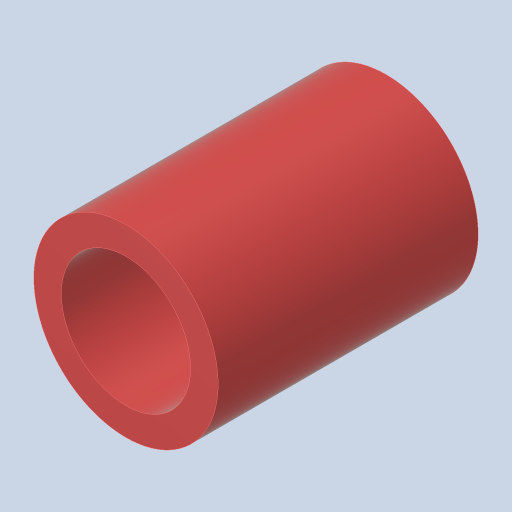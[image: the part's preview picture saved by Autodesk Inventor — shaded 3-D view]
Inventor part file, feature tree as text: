
AUTODESK INVENTOR PART (.ipt)
format: ipt  version: 2023.4 (Build 274418000, 418)  size: 122,880 bytes
history: native  units: in
note: dims shown in document units (in); Inventor stores cm internally (conversion verified against a paired STEP export)
features: extrude x1, sketch x1
ambient origin geometry x8: Origin, YZ Plane, XZ Plane, XY Plane, X Axis, Y Axis, Z Axis, Center Point
bodies: Solid1 (feature_tree)
feature tree (2):
  extrude  "Extrusion1"  Depth=1.178in
  sketch  "Sketch1"  dims[d0=0.585in d1=0.125in d2=1.178in d3=0.0in]
